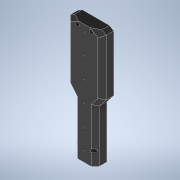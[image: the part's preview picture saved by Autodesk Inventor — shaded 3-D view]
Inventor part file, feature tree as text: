
AUTODESK INVENTOR PART (.ipt)
format: ipt  version: 2021 (Build 250183000, 183)  size: 322,048 bytes
history: native  units: mm
features: extrude x7, sketch x5, projected_geometry x5, chamfer x2, fillet x1
ambient origin geometry x8: Origin, YZ Plane, XZ Plane, XY Plane, X Axis, Y Axis, Z Axis, Center Point
bodies: Solid1 (feature_tree)
feature tree (20):
  extrude  "Extrusion1"  Depth=32.0mm
  extrude  "Extrusion3"  Depth=12.75mm
  sketch  "Sketch4"  dims[d8=85.966mm d9=39.718mm]
  extrude  "Extrusion4"  Depth=39.718mm
  extrude  "Extrusion5"  Depth=17.0mm TaperAngle=0.0deg
  chamfer  "Chamfer2"  Distance=6.0mm Angle=45.0deg
  chamfer  "Chamfer1"  Distance=15.0mm
  extrude  "Extrusion6"  Depth=4.0mm TaperAngle=45.0deg
  fillet  "Fillet1"  Radius=3.2mm
  extrude  "Extrusion13"  Depth=3.0mm
  extrude  "Extrusion14"  Depth=3.0mm
  sketch  "Sketch1"  dims[d0=76.484mm d1=32.0mm]
  sketch  "Sketch3"  dims[d3=10.2mm d4=12.75mm]
  projected_geometry  "Projected Loop1"
  projected_geometry  "Projected Loop2"
  projected_geometry  "Projected Loop3"
  projected_geometry  "Projected Loop4"
  projected_geometry  "Projected Loop5"
  sketch  "Sketch13"  dims[d10=25.967009mm d11=17.0mm d12=0.0mm d19=6.0mm d20=2.0mm d21=45.0deg]
  sketch  "Sketch14"  dims[d22=3.0mm d23=15.0mm d24=0.0mm d25=4.0mm d26=2.0mm d27=45.0deg d28=3.2mm d30=12.0mm d31=12.0mm d32=8.0mm d33=0.0mm d34=0.0mm d35=9.0mm d36=0.0mm d37=6.0mm d38=13.0mm d39=0.0mm d40=5.0mm d41=3.2mm d42=10.0mm d43=20.0mm d44=8.0mm d45=2.0mm d75=6.5mm d76=0.0mm d96=2.8mm d99=30.0mm d100=30.0mm d101=30.0mm d102=30.0mm d103=30.0mm d105=0.0mm d106=0.0mm d107=20.0mm d108=3.0mm d109=3.0mm d110=14.0mm d111=8.0mm d112=8.0mm d113=8.0mm d114=2.8mm d115=5.0mm d116=0.0mm]
